# Revit family: PT-LMZ460_Ver2021_230725
name_source: partatom
category: 通信装置
units: mm (PartAtom-declared; Revit-internal decimal feet)

## family parameters
OmniClass タイトル = Data/Multi/Media Projectors
OmniClass 番号 = 23.85.10.17.11.21
パーツ タイプ = 標準
ホスト = 面
ロード時にボイドで切り取り = はい
丸型コネクタ寸法 = 直径を使用
共有 = いいえ
注釈の向きを維持 = いいえ
部屋計算ポイント = いいえ

## types (6) — shared parameters
370_mm = High_Ceiling_Height : 370_mm
390_mm = High_Ceiling_Height : 390_mm
410_mm = High_Ceiling_Height : 410_mm
430_mm = High_Ceiling_Height : 430_mm
450_mm = High_Ceiling_Height : 450_mm
Body Depth = 309  [stored 1.01378 ft]
Ceiling Distance = 100  [stored 0.328084 ft]
Chip Quantity = 3
Clearance Value = 1000  [stored 3.28084 ft]
Const Length Projector Pan Handle = 2000  [stored 6.56168 ft]
Const Length Projector Panning Base = 1000  [stored 3.28084 ft]
Contrast Ratio = 3000000
Date Last Modified = 2022/6/3
Depth = 309  [stored 1.01378 ft]
Equipment Abbreviation = LVP
Family Version = 1.0.0
HDMI In = HDMI 19pin x 2 Deep Color, compatible with HDCP 1.4, 4K/30p signal input6 , CEC supported7 Audio Signal: Linear PCM (Sampling frequency: 48 kHz/44.1 kHz/32 kHz
Height = 105
LAN = RJ-45 x 1 for network control, 10Base-T, 100Base-TX, compatible with PJLinkTM (Class 2)
Lamp Life Economy = 24000
Lamp Life Full = 20000
Lamp Quantity = 2
Lamp Type = Laser diodes
Lens Type = Integrated
Market = Education
Model Disclaimer = Contact Panasonic for more information
Must be Level = No
Panasonic Logo Material = Paint - Panasonic Logo
Power Standby Eco = 1 W
Power Standby Normal = 14 W
Product Documentation Link = https://bizpartner.panasonic.net
Product Material = Plastic - Panasonic White
Product Page URL = https://panasonic.net
Provide Feedback = https://www.surveymonkey.com
Resolution Horizontal = 1920
Resolution Vertical = 1200
Technology = LCD™ chip x 3, LCD™ projection system
Temperature Max = 113 °F
Temperature Min = 32 °F
URL = http://panasonic.net
Weight = 9.30 lb
Width = 349  [stored 1.14501 ft]
製造元 = Panasonic
zero-valued in all types: 既定の高さ

## per-type parameters (varying)
| type | Brightness Economy | Brightness Full | Chip Diagonal | Heat Load Active | NO_LMW&LMZ | NO_LMW420 | NO_LMW460 | NO_LMX | NO_LMX420 | NO_LMX460 | NO_LMZ420 | NO_LMZ460 | Noise in High Mode | Noise in Low Mode | Part Description | Power Active | Total Rated Watts | 説明 |
| PT-LMW420 | 2940 lm | 4200 lm | 16.3 | 785.00 Btu/h | はい | はい | いいえ | いいえ | いいえ | いいえ | いいえ | いいえ | 33 | 23 | 4,200 lm, 16:10 Aspect Ratio, WXGA, Projector, PT-LMW420 | 230 W | 230 W | 4,200 lm, 16:10 Aspect Ratio, WXGA, Projector, PT-LMW420 |
| PT-LMW460 | 3220 lm | 4600 lm | 16.3 | 785.00 Btu/h | はい | いいえ | はい | いいえ | いいえ | いいえ | いいえ | いいえ | 35 | 24 | 4,600 lm, 16:10 Aspect Ratio, WXGA, Projector, PT-LMW460 | 230 W | 230 W | 4,600 lm, 16:10 Aspect Ratio, WXGA, Projector, PT-LMW460 |
| PT-LMX420 | 2940 lm | 4200 lm | 16 | 785.00 Btu/h | いいえ | いいえ | いいえ | はい | はい | いいえ | いいえ | いいえ | 33 | 23 | 4,200 lm, 4:3 Aspect Ratio, XGA, Projector, PT-LMX420 | 230 W | 230 W | 4,200 lm, 4:3 Aspect Ratio, XGA, Projector, PT-LMX420 |
| PT-LMX460 | 3220 lm | 4600 lm | 16 | 785.00 Btu/h | いいえ | いいえ | いいえ | はい | いいえ | はい | いいえ | いいえ | 35 | 24 | 4,600 lm, 4:3 Aspect Ratio, XGA, Projector, PT-LMX460 | 230 W | 230 W | 4,600 lm, 4:3 Aspect Ratio, XGA, Projector, PT-LMX460 |
| PT-LMZ420 | 2940 lm | 4200 lm | 16.3 | 820.00 Btu/h | はい | いいえ | いいえ | いいえ | いいえ | いいえ | はい | いいえ | 33 | 23 | 4,200 lm, 16:10 Aspect Ratio, WUXGA, Projector, PT-LMZ420 | 240 W | 240 W | 4,200 lm, 16:10 Aspect Ratio, WUXGA, Projector, PT-LMZ420 |
| PT-LMZ460 | 3220 lm | 4600 lm | 16.3 | 820.00 Btu/h | はい | いいえ | いいえ | いいえ | いいえ | いいえ | いいえ | はい | 35 | 24 | 4,600 lm, 16:10 Aspect Ratio, WUXGA, Projector, PT-LMZ460 | 240 W | 240 W | 4,600 lm, 16:10 Aspect Ratio, WUXGA, Projector, PT-LMZ460 |

note: column(s) folded — value = type name in every type: Part Number, モデル

note: [stored X ft] marks values corroborated as IEEE doubles in the binary element streams (Revit-internal decimal feet)

## geometry (parser evidence)
native form markers: Sweep x8
no freeform markers — native parametric forms only
